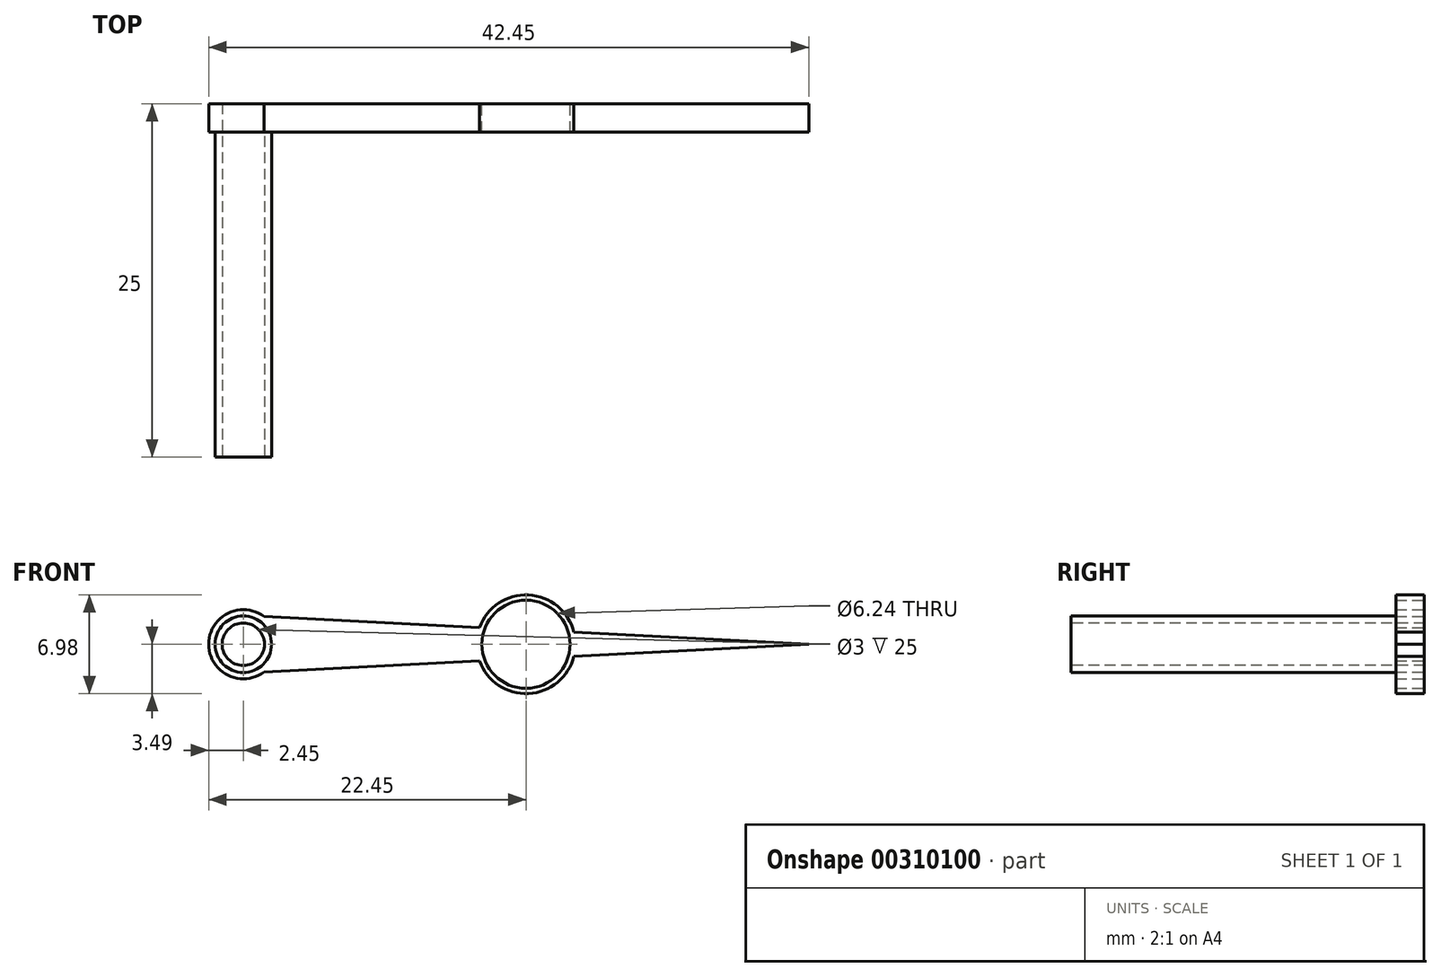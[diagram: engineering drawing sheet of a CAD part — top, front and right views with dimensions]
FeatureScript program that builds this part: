
annotation { "Feature Type Name" : "Feature", "Feature Type Description" : "" }
export const myFeature = defineFeature(function(context is Context, id is Id, definition is map)
    precondition{}
    {
        {
            var Q0;
            Q0=qCreatedBy(makeId("Front.planeOp"),FACE);
            var sketch = newSketch(context, id + "F0", { "sketchPlane" : qUnion([Q0])});
            skCircle(sketch, "E0", {"center": v(0, 0) * mm, "radius": 2.45 * mm});
            skLineSegment(sketch, "E1", {"start": v(0, 0) * mm, "end": v(40, 0) * mm, "construction": true});
            skLineSegment(sketch, "E2", {"start": v(1.48, 2.87) * mm, "end": v(1.48, -3.52) * mm, "construction": true});
            skLineSegment(sketch, "E3", {"start": v(1.48, 1.96) * mm, "end": v(16.71, 1.18) * mm});
            skLineSegment(sketch, "E4", {"start": v(40, 0) * mm, "end": v(23.39, -0.84) * mm});
            skCircle(sketch, "E5", {"center": v(20, 0) * mm, "radius": 3.5 * mm});
            skLineSegment(sketch, "E6.trimOffspring", {"start": v(23.39, 0.84) * mm, "end": v(40, 0) * mm});
            skLineSegment(sketch, "E7.trimOffspring", {"start": v(16.71, -1.18) * mm, "end": v(1.48, -1.96) * mm});
            skCircle(sketch, "E8", {"center": v(20, 0) * mm, "radius": 3.12 * mm});
            skSolve(sketch);
        }
        {
            var Q0;
            {var subQ0=sQuery(id+"F0.wireOp",EDGE,"E0");var subQ1=makeQuery(id+"F0.imprint","INTERSECT",VERTEX,{"derivedFrom":[subQ0,sQuery(id+"F0.wireOp",EDGE,"E3")]});Q0=makeQuery(id+"F0.imprint","IMPRINT",FACE,{"disambiguationData":[TD([[makeQuery(id+"F0.imprint","IMPRINT",EDGE,{"disambiguationData":[TD([[subQ1,-1.0]])],"derivedFrom":subQ0}),1.0]])]});}
            var Q1;
            {var subQ0=sQuery(id+"F0.wireOp",EDGE,"E3");Q1=makeQuery(id+"F0.imprint","IMPRINT",FACE,{"disambiguationData":[TD([[makeQuery(id+"F0.imprint","IMPRINT",EDGE,{"derivedFrom":subQ0}),-1.0]])]});}
            var Q2;
            {var subQ0=sQuery(id+"F0.wireOp",EDGE,"E5");var subQ1=makeQuery(id+"F0.imprint","INTERSECT",VERTEX,{"derivedFrom":[sQuery(id+"F0.wireOp",EDGE,"E3"),subQ0]});Q2=makeQuery(id+"F0.imprint","IMPRINT",FACE,{"disambiguationData":[TD([[makeQuery(id+"F0.imprint","IMPRINT",EDGE,{"disambiguationData":[TD([[subQ1,1.0]])],"derivedFrom":subQ0}),1.0]])]});}
            var Q3;
            {var subQ0=sQuery(id+"F0.wireOp",EDGE,"E4");Q3=makeQuery(id+"F0.imprint","IMPRINT",FACE,{"disambiguationData":[TD([[makeQuery(id+"F0.imprint","IMPRINT",EDGE,{"derivedFrom":subQ0}),-1.0]])]});}
            extrude(context, id + "F1", {"entities" : qUnion([Q0, Q1, Q2, Q3]), "endBound" : BoundingType.SYMMETRIC, "depth" : 2 * mm});
        }
        {
            var Q0;
            Q0=makeQuery(id+"F1.opExtrude","CAP_FACE",FACE,{"disambiguationData":[OSD([sQuery(id+"F0.wireOp",EDGE,"E0"),sQuery(id+"F0.wireOp",EDGE,"E3"),sQuery(id+"F0.wireOp",EDGE,"E4"),sQuery(id+"F0.wireOp",EDGE,"E5"),sQuery(id+"F0.wireOp",EDGE,"E6.trimOffspring"),sQuery(id+"F0.wireOp",EDGE,"E7.trimOffspring"),sQuery(id+"F0.wireOp",EDGE,"E8")])],"isStart":true});
            var sketch = newSketch(context, id + "F2", { "sketchPlane" : qUnion([Q0])});
            skCircle(sketch, "E9", {"center": v(0, 0) * mm, "radius": 2 * mm});
            skSolve(sketch);
        }
        {
            var Q0;
            Q0=makeQuery(id+"F2.imprint","IMPRINT",FACE,{"disambiguationData":[TD([[makeQuery(id+"F2.imprint","IMPRINT",EDGE,{"derivedFrom":sQuery(id+"F2.wireOp",EDGE,"E9")}),1.0]])]});
            extrude(context, id + "F3", {"entities" : qUnion([Q0]), "operationType" : NewBodyOperationType.ADD, "oppositeDirection" : true, "depth" : 25 * mm});
        }
        {
            var Q0;
            Q0=makeQuery(id+"F3.opExtrude","CAP_FACE",FACE,{"disambiguationData":[OSD([sQuery(id+"F2.wireOp",EDGE,"E9")])],"isStart":false});
            var sketch = newSketch(context, id + "F4", { "sketchPlane" : qUnion([Q0])});
            skCircle(sketch, "E10", {"center": v(0, 0) * mm, "radius": 1.5 * mm});
            skSolve(sketch);
        }
        {
            var Q0;
            Q0 = qSketchRegion(id + "F4", true);
            extrude(context, id + "F5", {"entities" : qUnion([Q0]), "operationType" : NewBodyOperationType.REMOVE, "oppositeDirection" : true, "depth" : 25 * mm});
        }
    });
